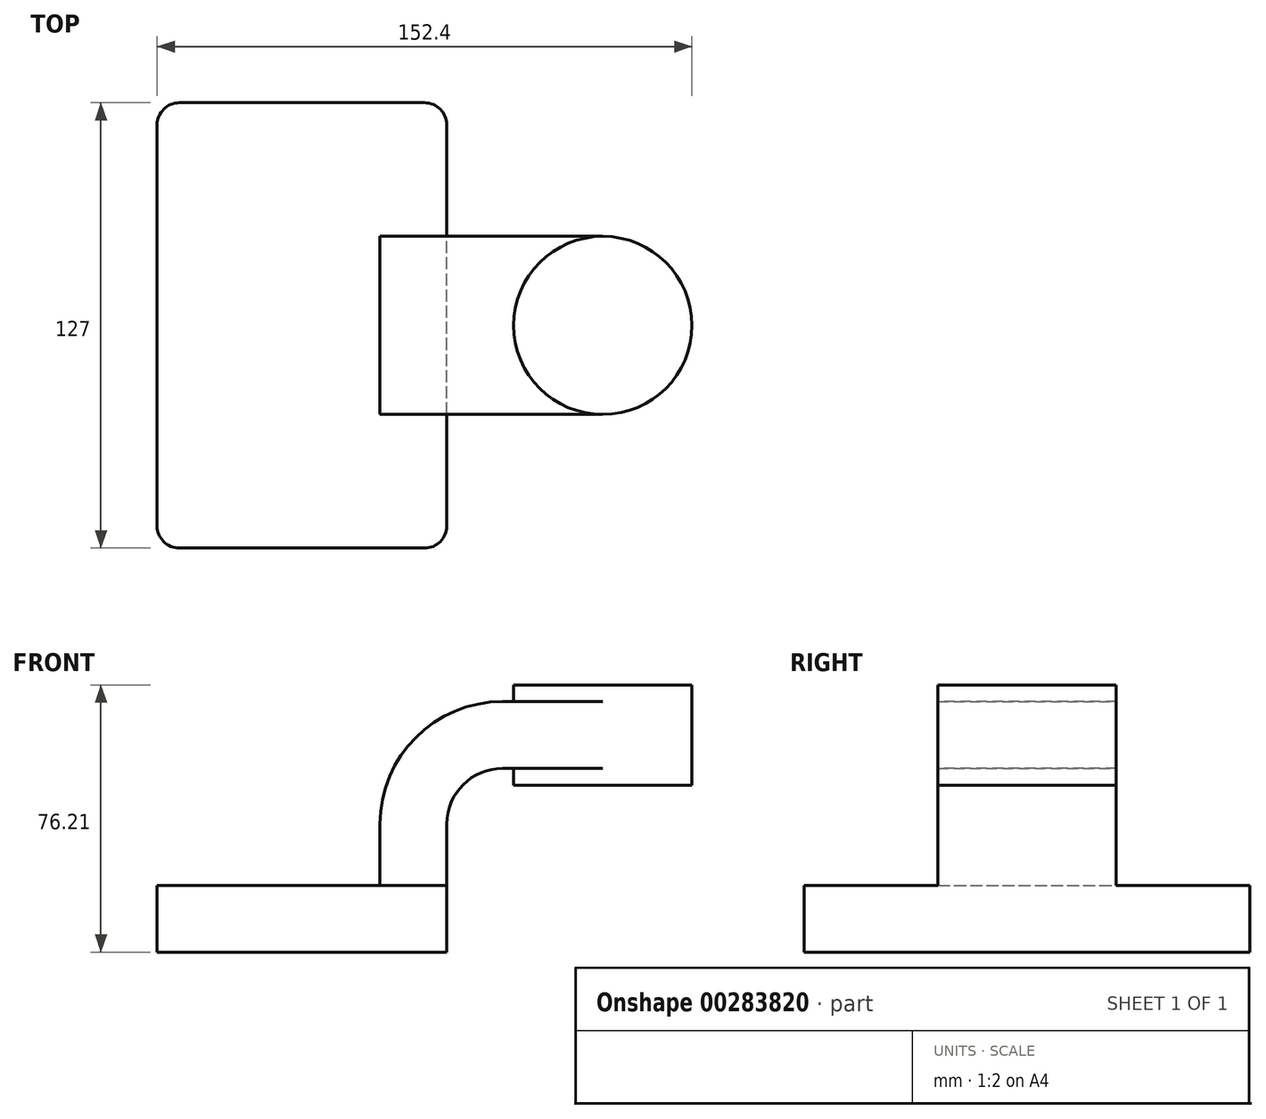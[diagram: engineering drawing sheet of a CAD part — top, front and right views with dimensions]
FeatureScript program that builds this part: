
annotation { "Feature Type Name" : "Feature", "Feature Type Description" : "" }
export const myFeature = defineFeature(function(context is Context, id is Id, definition is map)
    precondition{}
    {
        {
            var Q0;
            Q0=qCreatedBy(makeId("Front.planeOp"),FACE);
            var sketch = newSketch(context, id + "F0", { "sketchPlane" : qUnion([Q0])});
            skLineSegment(sketch, "E0.bottom", {"start": v(-41.28, -9.52) * mm, "end": v(41.28, -9.53) * mm});
            skLineSegment(sketch, "E0.top", {"start": v(-41.28, 9.52) * mm, "end": v(41.28, 9.52) * mm});
            skLineSegment(sketch, "E0.left", {"start": v(-41.28, -9.52) * mm, "end": v(-41.28, 9.53) * mm});
            skLineSegment(sketch, "E0.right", {"start": v(41.28, -9.53) * mm, "end": v(41.28, 9.52) * mm});
            skPoint(sketch, "E0.middle", {"position": v(0, 0) * mm});
            skLineSegment(sketch, "E1.bottom", {"start": v(60.32, 38.1) * mm, "end": v(111.12, 38.1) * mm});
            skLineSegment(sketch, "E1.top", {"start": v(60.32, 66.67) * mm, "end": v(111.12, 66.67) * mm});
            skLineSegment(sketch, "E1.left", {"start": v(60.32, 38.1) * mm, "end": v(60.32, 66.67) * mm});
            skLineSegment(sketch, "E1.right", {"start": v(111.12, 38.1) * mm, "end": v(111.12, 66.67) * mm});
            skPoint(sketch, "E1.middle", {"position": v(85.72, 52.39) * mm});
            skLineSegment(sketch, "E2", {"start": v(41.28, 9.52) * mm, "end": v(41.28, 26.99) * mm});
            skArc(sketch, "E3", {"start": v(41.28, 26.99) * mm, "mid": v(45.92, 38.21) * mm, "end": v(57.15, 42.86) * mm});
            skLineSegment(sketch, "E4", {"start": v(57.15, 42.86) * mm, "end": v(85.72, 42.86) * mm});
            skLineSegment(sketch, "E5.0", {"start": v(57.15, 61.91) * mm, "end": v(85.72, 61.91) * mm});
            skArc(sketch, "E5.1", {"start": v(22.23, 26.99) * mm, "mid": v(32.45, 51.68) * mm, "end": v(57.15, 61.91) * mm});
            skLineSegment(sketch, "E5.2", {"start": v(22.23, 9.52) * mm, "end": v(22.23, 26.99) * mm});
            skLineSegment(sketch, "E6", {"start": v(85.72, 42.86) * mm, "end": v(85.72, 61.91) * mm});
            skFitSpline(sketch, "E7", {"points": [v(-41.28, 9.53) * mm, v(57.15, 61.91) * mm], "startDerivative": vector(0, 100.5) * mm, "endDerivative": vector(143.98, 0) * mm});
            skPoint(sketch, "E8", {"position": v(71.44, 61.91) * mm});
            skPoint(sketch, "E9", {"position": v(-41.28, 0) * mm});
            skLineSegment(sketch, "E10", {"start": v(85.72, 66.67) * mm, "end": v(85.72, 42.86) * mm});
            skLineSegment(sketch, "E11", {"start": v(85.72, 42.86) * mm, "end": v(85.72, 38.1) * mm});
            skSolve(sketch);
        }
        {
            var Q0;
            Q0=makeQuery(id+"F0.imprint","IMPRINT",FACE,{"disambiguationData":[TD([[makeQuery(id+"F0.imprint","IMPRINT",EDGE,{"derivedFrom":sQuery(id+"F0.wireOp",EDGE,"E0.bottom")}),1.0]])]});
            extrude(context, id + "F1", {"entities" : qUnion([Q0]), "endBound" : BoundingType.SYMMETRIC, "depth" : 127 * mm});
        }
        {
            var Q0;
            {var subQ1=sQuery(id+"F0.wireOp",EDGE,"E2");Q0=makeQuery(id+"F0.imprint","IMPRINT",FACE,{"disambiguationData":[TD([[makeQuery(id+"F0.imprint","IMPRINT",EDGE,{"derivedFrom":subQ1}),1.0]])]});}
            var Q1;
            {var subQ0=sQuery(id+"F0.wireOp",EDGE,"E4");var subQ1=sQuery(id+"F0.wireOp",EDGE,"E1.left");var subQ2=makeQuery(id+"F0.imprint","INTERSECT",VERTEX,{"derivedFrom":[subQ1,subQ0]});Q1=makeQuery(id+"F0.imprint","IMPRINT",FACE,{"disambiguationData":[TD([[makeQuery(id+"F0.imprint","IMPRINT",EDGE,{"disambiguationData":[TD([[subQ2,-1.0]])],"derivedFrom":subQ1}),-1.0]])]});}
            extrude(context, id + "F2", {"entities" : qUnion([Q0, Q1]), "operationType" : NewBodyOperationType.ADD, "endBound" : BoundingType.SYMMETRIC, "depth" : 50.8 * mm});
        }
        {
            var Q0;
            Q0=makeQuery(id+"F0.imprint","IMPRINT",FACE,{"disambiguationData":[TD([[makeQuery(id+"F0.imprint","IMPRINT",EDGE,{"derivedFrom":sQuery(id+"F0.wireOp",EDGE,"E5.1")}),1.0]])]});
            extrude(context, id + "F3", {"entities" : qUnion([Q0]), "operationType" : NewBodyOperationType.ADD, "endBound" : BoundingType.SYMMETRIC, "depth" : 15.88 * mm});
        }
        {
            var Q0;
            {var subQ4=sQuery(id+"F0.wireOp",EDGE,"E1.right");Q0=makeQuery(id+"F0.imprint","IMPRINT",FACE,{"disambiguationData":[TD([[makeQuery(id+"F0.imprint","IMPRINT",EDGE,{"derivedFrom":subQ4}),1.0]])]});}
            var Q1;
            Q1=sQuery(id+"F0.wireOp",EDGE,"E10");
            revolve(context, id + "F4", {"operationType" : NewBodyOperationType.ADD, "entities" : qUnion([Q0]), "axis" : qUnion([Q1]), "revolveType" : RevolveType.FULL});
        }
        {
            var Q0;
            Q0=makeQuery(id+"F1.opExtrude","CAP_EDGE",EDGE,{"disambiguationData":[OSD([sQuery(id+"F0.wireOp",EDGE,"E0.right")])],"isStart":false});
            var Q1;
            Q1=makeQuery(id+"F1.opExtrude","CAP_EDGE",EDGE,{"disambiguationData":[OSD([sQuery(id+"F0.wireOp",EDGE,"E0.left")])],"isStart":false});
            var Q2;
            Q2=makeQuery(id+"F1.opExtrude","CAP_EDGE",EDGE,{"disambiguationData":[OSD([sQuery(id+"F0.wireOp",EDGE,"E0.left")])],"isStart":true});
            var Q3;
            Q3=makeQuery(id+"F1.opExtrude","CAP_EDGE",EDGE,{"disambiguationData":[OSD([sQuery(id+"F0.wireOp",EDGE,"E0.right")])],"isStart":true});
            fillet(context, id + "F5", {"entities" : qUnion([Q0, Q1, Q2, Q3]), "radius" : 6.35 * mm, "tangentPropagation" : true, "allowEdgeOverflow" : false});
        }
    });
